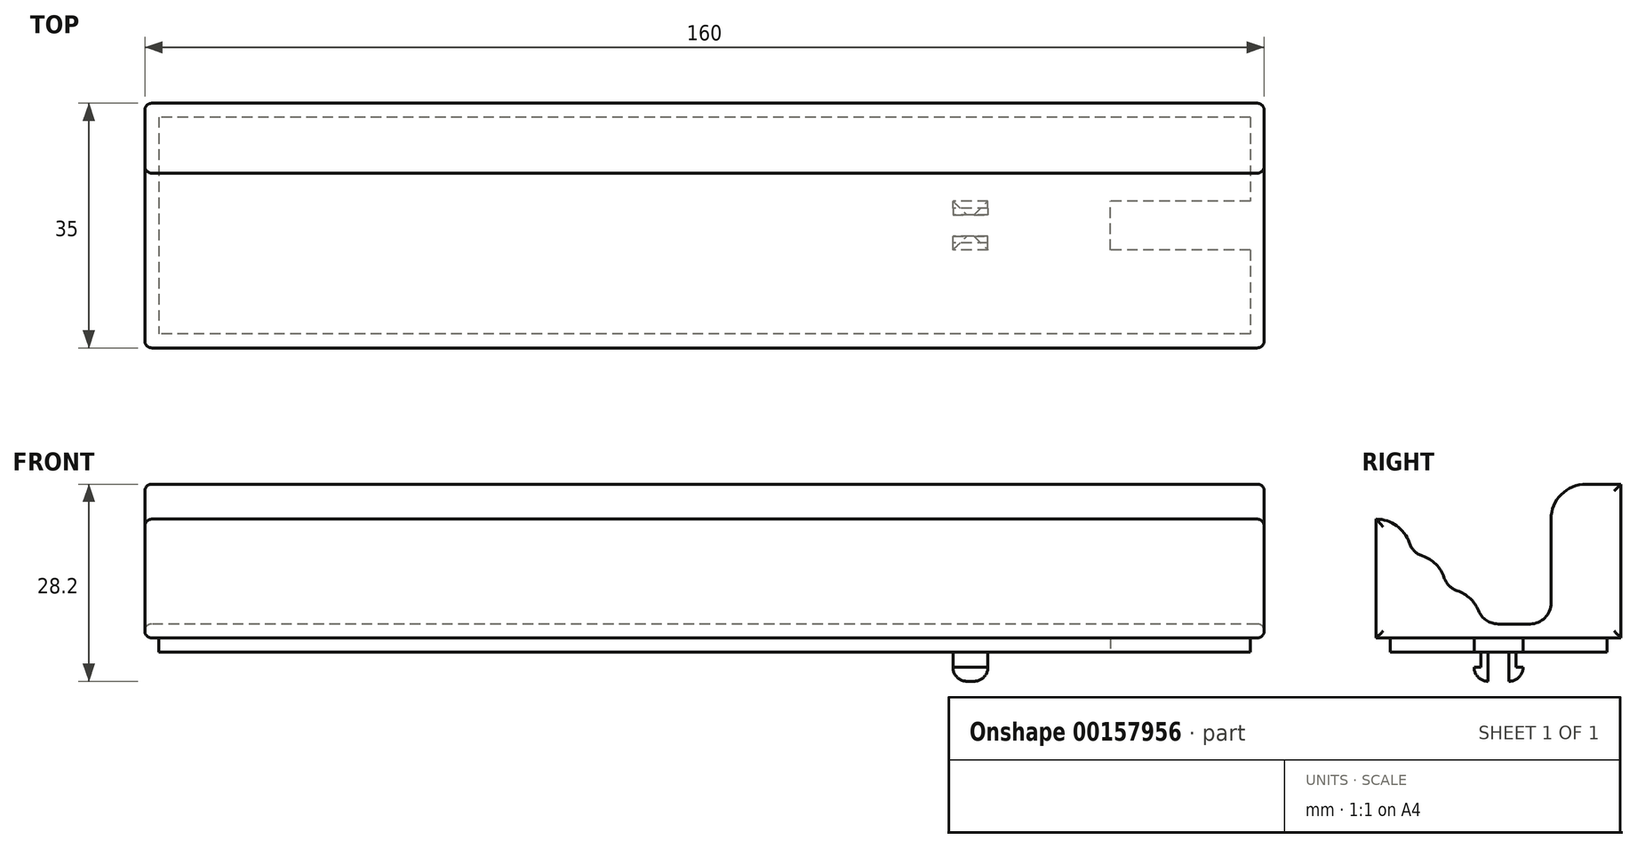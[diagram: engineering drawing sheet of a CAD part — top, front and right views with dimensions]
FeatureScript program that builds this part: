
annotation { "Feature Type Name" : "Feature", "Feature Type Description" : "" }
export const myFeature = defineFeature(function(context is Context, id is Id, definition is map)
    precondition{}
    {
        {
            var Q0;
            Q0=qCreatedBy(makeId("Right.planeOp"),FACE);
            var sketch = newSketch(context, id + "F0", { "sketchPlane" : qUnion([Q0])});
            skPoint(sketch, "E0.middle", {"position": v(0, 0) * mm});
            skLineSegment(sketch, "E1", {"start": v(18.73, 20.16) * mm, "end": v(18.73, 20.16) * mm});
            skLineSegment(sketch, "E2.bottom", {"start": v(13.13, 38.98) * mm, "end": v(22.1, 38.98) * mm});
            skPoint(sketch, "E3.visualSharp", {"position": v(11.13, 38.98) * mm});
            skArc(sketch, "E3.filletArc", {"start": v(13.13, 38.98) * mm, "mid": v(11.72, 38.4) * mm, "end": v(11.13, 36.98) * mm});
            skLineSegment(sketch, "E4.bottom", {"start": v(17.5, 1) * mm, "end": v(-17.5, 1) * mm});
            skLineSegment(sketch, "E4.top", {"start": v(17.5, -1) * mm, "end": v(-17.5, -1) * mm});
            skLineSegment(sketch, "E4.left", {"start": v(17.5, 1) * mm, "end": v(17.5, -1) * mm});
            skLineSegment(sketch, "E4.right", {"start": v(-17.5, 1) * mm, "end": v(-17.5, -1) * mm});
            skLineSegment(sketch, "E5.bottom", {"start": v(17.5, 1) * mm, "end": v(7.5, 1) * mm});
            skLineSegment(sketch, "E5.top", {"start": v(17.5, 21) * mm, "end": v(12.5, 21) * mm});
            skLineSegment(sketch, "E5.left", {"start": v(17.5, 1) * mm, "end": v(17.5, 21) * mm});
            skLineSegment(sketch, "E5.right", {"start": v(7.5, 1) * mm, "end": v(7.5, 16) * mm});
            skLineSegment(sketch, "E6.bottom", {"start": v(-17.5, 1) * mm, "end": v(-12.5, 1) * mm});
            skLineSegment(sketch, "E6.top", {"start": v(-17.5, 16) * mm, "end": v(-17.5, 16) * mm});
            skLineSegment(sketch, "E6.left", {"start": v(-17.5, 1) * mm, "end": v(-17.5, 16) * mm});
            skLineSegment(sketch, "E6.right", {"start": v(-12.5, 1) * mm, "end": v(-12.5, 11) * mm});
            skLineSegment(sketch, "E7.bottom", {"start": v(-12.5, 11) * mm, "end": v(-12.5, 11) * mm});
            skLineSegment(sketch, "E7.top", {"start": v(-12.5, 1) * mm, "end": v(-7.5, 1) * mm});
            skLineSegment(sketch, "E7.left", {"start": v(-12.5, 11) * mm, "end": v(-12.5, 1) * mm});
            skLineSegment(sketch, "E7.right", {"start": v(-7.5, 6) * mm, "end": v(-7.5, 1) * mm});
            skLineSegment(sketch, "E8.bottom", {"start": v(-7.5, 6) * mm, "end": v(-7.5, 6) * mm});
            skLineSegment(sketch, "E8.top", {"start": v(-7.5, 1) * mm, "end": v(-2.5, 1) * mm});
            skLineSegment(sketch, "E8.right", {"start": v(-2.5, 1) * mm, "end": v(-2.5, 1) * mm});
            skPoint(sketch, "E9.visualSharp", {"position": v(7.5, 21) * mm});
            skArc(sketch, "E9.filletArc", {"start": v(12.5, 21) * mm, "mid": v(8.96, 19.54) * mm, "end": v(7.5, 16) * mm});
            skPoint(sketch, "E10.visualSharp", {"position": v(-2.5, 6) * mm});
            skArc(sketch, "E10.filletArc", {"start": v(-2.5, 1) * mm, "mid": v(-3.96, 4.54) * mm, "end": v(-7.5, 6) * mm});
            skPoint(sketch, "E11.visualSharp", {"position": v(-7.5, 11) * mm});
            skArc(sketch, "E11.filletArc", {"start": v(-7.5, 6) * mm, "mid": v(-8.96, 9.54) * mm, "end": v(-12.5, 11) * mm});
            skPoint(sketch, "E12.visualSharp", {"position": v(-12.5, 16) * mm});
            skArc(sketch, "E12.filletArc", {"start": v(-12.5, 11) * mm, "mid": v(-13.96, 14.54) * mm, "end": v(-17.5, 16) * mm});
            skSolve(sketch);
        }
        {
            var Q0;
            Q0=makeQuery(id+"F0.imprint","IMPRINT",FACE,{"disambiguationData":[TD([[makeQuery(id+"F0.imprint","IMPRINT",EDGE,{"derivedFrom":sQuery(id+"F0.wireOp",EDGE,"E5.top")}),1.0]])]});
            var Q1;
            Q1=makeQuery(id+"F0.imprint","IMPRINT",FACE,{"disambiguationData":[TD([[makeQuery(id+"F0.imprint","IMPRINT",EDGE,{"derivedFrom":sQuery(id+"F0.wireOp",EDGE,"E4.top")}),-1.0]])]});
            var Q2;
            {var subQ0=sQuery(id+"F0.wireOp",EDGE,"E6.left");Q2=makeQuery(id+"F0.imprint","IMPRINT",FACE,{"disambiguationData":[TD([[makeQuery(id+"F0.imprint","IMPRINT",EDGE,{"derivedFrom":subQ0}),-1.0]])]});}
            var Q3;
            {var subQ2=sQuery(id+"F0.wireOp",EDGE,"E6.right");Q3=makeQuery(id+"F0.imprint","IMPRINT",FACE,{"disambiguationData":[TD([[makeQuery(id+"F0.imprint","IMPRINT",EDGE,{"derivedFrom":subQ2}),-1.0]])]});}
            var Q4;
            {var subQ0=sQuery(id+"F0.wireOp",EDGE,"E7.right");Q4=makeQuery(id+"F0.imprint","IMPRINT",FACE,{"disambiguationData":[TD([[makeQuery(id+"F0.imprint","IMPRINT",EDGE,{"derivedFrom":subQ0}),1.0]])]});}
            extrude(context, id + "F1", {"entities" : qUnion([Q0, Q1, Q2, Q3, Q4]), "endBound" : BoundingType.SYMMETRIC, "depth" : 160 * mm});
        }
        {
            var Q0;
            Q0=makeQuery(id+"F1.opExtrude","SWEPT_FACE",FACE,{"disambiguationData":[OSD([sQuery(id+"F0.wireOp",EDGE,"E4.top")])]});
            var sketch = newSketch(context, id + "F2", { "sketchPlane" : qUnion([Q0])});
            skLineSegment(sketch, "E13.bottom", {"start": v(78, -15.5) * mm, "end": v(-78, -15.5) * mm});
            skLineSegment(sketch, "E13.top", {"start": v(78, 15.5) * mm, "end": v(-78, 15.5) * mm});
            skLineSegment(sketch, "E13.left", {"start": v(78, -15.5) * mm, "end": v(78, 15.5) * mm});
            skLineSegment(sketch, "E13.right", {"start": v(-78, -15.5) * mm, "end": v(-78, 15.5) * mm});
            skPoint(sketch, "E13.middle", {"position": v(0, 0) * mm});
            skSolve(sketch);
        }
        {
            var Q0;
            Q0=qSketchRegion(id+"F2",true);
            extrude(context, id + "F3", {"entities" : qUnion([Q0]), "operationType" : NewBodyOperationType.ADD, "depth" : 2 * mm});
        }
        {
            var Q0;
            Q0=makeQuery(id+"F3.opExtrude","CAP_FACE",FACE,{"disambiguationData":[OSD([sQuery(id+"F2.wireOp",EDGE,"E13.bottom"),sQuery(id+"F2.wireOp",EDGE,"E13.top"),sQuery(id+"F2.wireOp",EDGE,"E13.left"),sQuery(id+"F2.wireOp",EDGE,"E13.right")])],"isStart":false});
            var sketch = newSketch(context, id + "F4", { "sketchPlane" : qUnion([Q0])});
            skLineSegment(sketch, "E14.bottom", {"start": v(40.5, -2.5) * mm, "end": v(35.5, -2.5) * mm});
            skLineSegment(sketch, "E14.top", {"start": v(40.5, 2.5) * mm, "end": v(35.5, 2.5) * mm});
            skLineSegment(sketch, "E14.left", {"start": v(40.5, -2.5) * mm, "end": v(40.5, 2.5) * mm});
            skLineSegment(sketch, "E14.right", {"start": v(35.5, -2.5) * mm, "end": v(35.5, 2.5) * mm});
            skPoint(sketch, "E14.middle", {"position": v(38, 0) * mm});
            skPoint(sketch, "E15", {"position": v(78, -0.48) * mm});
            skSolve(sketch);
        }
        {
            var Q0;
            Q0=qSketchRegion(id+"F4",true);
            extrude(context, id + "F5", {"entities" : qUnion([Q0]), "operationType" : NewBodyOperationType.ADD, "depth" : 2.2 * mm});
        }
        {
            var Q0;
            Q0=makeQuery(id+"F5.opExtrude","CAP_FACE",FACE,{"disambiguationData":[OSD([sQuery(id+"F4.wireOp",EDGE,"E14.bottom"),sQuery(id+"F4.wireOp",EDGE,"E14.top"),sQuery(id+"F4.wireOp",EDGE,"E14.left"),sQuery(id+"F4.wireOp",EDGE,"E14.right")])],"isStart":false});
            var sketch = newSketch(context, id + "F6", { "sketchPlane" : qUnion([Q0])});
            skLineSegment(sketch, "E16.bottom", {"start": v(40.5, 3.5) * mm, "end": v(35.5, 3.5) * mm});
            skLineSegment(sketch, "E16.top", {"start": v(40.5, -3.5) * mm, "end": v(35.5, -3.5) * mm});
            skLineSegment(sketch, "E16.left", {"start": v(35.5, 3.5) * mm, "end": v(35.5, -3.5) * mm});
            skLineSegment(sketch, "E16.right", {"start": v(40.5, 3.5) * mm, "end": v(40.5, -3.5) * mm});
            skPoint(sketch, "E16.middle.positionSnap0", {"position": v(40.5, 0) * mm});
            skPoint(sketch, "E16.centerSnap0", {"position": v(40.5, 0) * mm});
            skPoint(sketch, "E17", {"position": v(35.5, 0) * mm});
            skSolve(sketch);
        }
        {
            var Q0;
            Q0=qSketchRegion(id+"F6",true);
            extrude(context, id + "F7", {"entities" : qUnion([Q0]), "operationType" : NewBodyOperationType.ADD, "depth" : 2 * mm});
        }
        {
            var Q0;
            Q0=makeQuery(id+"F7.opExtrude","CAP_FACE",FACE,{"disambiguationData":[OSD([sQuery(id+"F6.wireOp",EDGE,"E16.bottom"),sQuery(id+"F6.wireOp",EDGE,"E16.top"),sQuery(id+"F6.wireOp",EDGE,"E16.left"),sQuery(id+"F6.wireOp",EDGE,"E16.right")])],"isStart":false});
            var sketch = newSketch(context, id + "F8", { "sketchPlane" : qUnion([Q0])});
            skLineSegment(sketch, "E18.bottom", {"start": v(40.5, 1.5) * mm, "end": v(35.5, 1.5) * mm});
            skLineSegment(sketch, "E18.top", {"start": v(40.5, -1.5) * mm, "end": v(35.5, -1.5) * mm});
            skLineSegment(sketch, "E18.left", {"start": v(35.5, 1.5) * mm, "end": v(35.5, -1.5) * mm});
            skLineSegment(sketch, "E18.right", {"start": v(40.5, 1.5) * mm, "end": v(40.5, -1.5) * mm});
            skLineSegment(sketch, "E19.bottom", {"start": v(39.5, -3.5) * mm, "end": v(36.5, -3.5) * mm});
            skSolve(sketch);
        }
        {
            var Q0;
            Q0=makeQuery(id+"F8.imprint","IMPRINT",FACE,{"disambiguationData":[TD([[makeQuery(id+"F8.imprint","IMPRINT",EDGE,{"derivedFrom":sQuery(id+"F8.wireOp",EDGE,"E18.bottom")}),1.0]])]});
            extrude(context, id + "F9", {"entities" : qUnion([Q0]), "operationType" : NewBodyOperationType.REMOVE, "oppositeDirection" : true, "depth" : 4.2 * mm});
        }
        {
            var Q0;
            {var subQ0=sQuery(id+"F6.wireOp",EDGE,"E16.right");var subQ1=sQuery(id+"F6.wireOp",EDGE,"E16.top");var subQ3=makeQuery(id+"F7.opExtrude","CAP_EDGE",EDGE,{"disambiguationData":[OSD([subQ0])],"isStart":false});Q0=makeQuery(id+"F9.boolean.opBoolean","SPLIT",EDGE,{"disambiguationData":[TD([makeQuery(id+"F7.opExtrude","SWEPT_FACE",FACE,{"disambiguationData":[OSD([subQ1])]})])],"derivedFrom":subQ3});}
            var Q1;
            {var subQ0=sQuery(id+"F6.wireOp",EDGE,"E16.right");var subQ1=sQuery(id+"F6.wireOp",EDGE,"E16.top");var subQ3=makeQuery(id+"F7.opExtrude","CAP_EDGE",EDGE,{"disambiguationData":[OSD([subQ1])],"isStart":false});Q1=makeQuery(id+"F9.boolean.opBoolean","SPLIT",EDGE,{"disambiguationData":[TD([makeQuery(id+"F7.opExtrude","SWEPT_FACE",FACE,{"disambiguationData":[OSD([subQ0])]})])],"derivedFrom":subQ3});}
            var Q2;
            {var subQ0=sQuery(id+"F6.wireOp",EDGE,"E16.bottom");var subQ1=sQuery(id+"F6.wireOp",EDGE,"E16.right");var subQ3=makeQuery(id+"F7.opExtrude","CAP_EDGE",EDGE,{"disambiguationData":[OSD([subQ1])],"isStart":false});Q2=makeQuery(id+"F9.boolean.opBoolean","SPLIT",EDGE,{"disambiguationData":[TD([makeQuery(id+"F7.opExtrude","SWEPT_FACE",FACE,{"disambiguationData":[OSD([subQ0])]})])],"derivedFrom":subQ3});}
            var Q3;
            {var subQ0=sQuery(id+"F6.wireOp",EDGE,"E16.bottom");var subQ1=sQuery(id+"F6.wireOp",EDGE,"E16.right");var subQ3=makeQuery(id+"F7.opExtrude","CAP_EDGE",EDGE,{"disambiguationData":[OSD([subQ0])],"isStart":false});Q3=makeQuery(id+"F9.boolean.opBoolean","SPLIT",EDGE,{"disambiguationData":[TD([makeQuery(id+"F7.opExtrude","SWEPT_FACE",FACE,{"disambiguationData":[OSD([subQ1])]})])],"derivedFrom":subQ3});}
            var Q4;
            {var subQ0=sQuery(id+"F6.wireOp",EDGE,"E16.bottom");var subQ1=sQuery(id+"F6.wireOp",EDGE,"E16.left");var subQ3=makeQuery(id+"F7.opExtrude","CAP_EDGE",EDGE,{"disambiguationData":[OSD([subQ0])],"isStart":false});Q4=makeQuery(id+"F9.boolean.opBoolean","SPLIT",EDGE,{"disambiguationData":[TD([makeQuery(id+"F7.opExtrude","SWEPT_FACE",FACE,{"disambiguationData":[OSD([subQ1])]})])],"derivedFrom":subQ3});}
            var Q5;
            {var subQ0=sQuery(id+"F6.wireOp",EDGE,"E16.bottom");var subQ1=sQuery(id+"F6.wireOp",EDGE,"E16.left");var subQ3=makeQuery(id+"F7.opExtrude","CAP_EDGE",EDGE,{"disambiguationData":[OSD([subQ1])],"isStart":false});Q5=makeQuery(id+"F9.boolean.opBoolean","SPLIT",EDGE,{"disambiguationData":[TD([makeQuery(id+"F7.opExtrude","SWEPT_FACE",FACE,{"disambiguationData":[OSD([subQ0])]})])],"derivedFrom":subQ3});}
            var Q6;
            {var subQ0=sQuery(id+"F6.wireOp",EDGE,"E16.left");var subQ1=sQuery(id+"F6.wireOp",EDGE,"E16.top");var subQ3=makeQuery(id+"F7.opExtrude","CAP_EDGE",EDGE,{"disambiguationData":[OSD([subQ0])],"isStart":false});Q6=makeQuery(id+"F9.boolean.opBoolean","SPLIT",EDGE,{"disambiguationData":[TD([makeQuery(id+"F7.opExtrude","SWEPT_FACE",FACE,{"disambiguationData":[OSD([subQ1])]})])],"derivedFrom":subQ3});}
            var Q7;
            {var subQ0=sQuery(id+"F6.wireOp",EDGE,"E16.left");var subQ1=sQuery(id+"F6.wireOp",EDGE,"E16.top");var subQ3=makeQuery(id+"F7.opExtrude","CAP_EDGE",EDGE,{"disambiguationData":[OSD([subQ1])],"isStart":false});Q7=makeQuery(id+"F9.boolean.opBoolean","SPLIT",EDGE,{"disambiguationData":[TD([makeQuery(id+"F7.opExtrude","SWEPT_FACE",FACE,{"disambiguationData":[OSD([subQ0])]})])],"derivedFrom":subQ3});}
            fillet(context, id + "F10", {"entities" : qUnion([Q0, Q1, Q2, Q3, Q4, Q5, Q6, Q7]), "radius" : 2 * mm, "tangentPropagation" : true, "allowEdgeOverflow" : false});
        }
        {
            var Q0;
            Q0=makeQuery(id+"F9.boolean.opBoolean","MERGE",FACE,{"derivedFrom":[makeQuery(id+"F3.opExtrude","CAP_FACE",FACE,{"disambiguationData":[OSD([sQuery(id+"F2.wireOp",EDGE,"E13.bottom"),sQuery(id+"F2.wireOp",EDGE,"E13.top"),sQuery(id+"F2.wireOp",EDGE,"E13.left"),sQuery(id+"F2.wireOp",EDGE,"E13.right")])],"isStart":false}),makeQuery(id+"F9.opExtrude","CAP_FACE",FACE,{"disambiguationData":[OSD([sQuery(id+"F8.wireOp",EDGE,"E18.bottom"),sQuery(id+"F8.wireOp",EDGE,"E18.top"),sQuery(id+"F8.wireOp",EDGE,"E18.left"),sQuery(id+"F8.wireOp",EDGE,"E18.right")])],"isStart":false})]});
            var sketch = newSketch(context, id + "F11", { "sketchPlane" : qUnion([Q0])});
            skLineSegment(sketch, "E20.bottom", {"start": v(78, 3.5) * mm, "end": v(58, 3.5) * mm});
            skLineSegment(sketch, "E20.top", {"start": v(78, -3.5) * mm, "end": v(58, -3.5) * mm});
            skLineSegment(sketch, "E20.left", {"start": v(78, 3.5) * mm, "end": v(78, -3.5) * mm});
            skLineSegment(sketch, "E20.right", {"start": v(58, 3.5) * mm, "end": v(58, -3.5) * mm});
            skPoint(sketch, "E20.middle", {"position": v(68, 0) * mm});
            skSolve(sketch);
        }
        {
            var Q0;
            Q0=qSketchRegion(id+"F11",true);
            extrude(context, id + "F12", {"entities" : qUnion([Q0]), "operationType" : NewBodyOperationType.REMOVE, "oppositeDirection" : true, "depth" : 2 * mm});
        }
        {
            var Q0;
            Q0=makeQuery(id+"F1.opExtrude","SWEPT_EDGE",EDGE,{"disambiguationData":[OSD([sQuery(id+"F0.wireOp",EDGE,"E6.right"),sQuery(id+"F0.wireOp",EDGE,"E11.filletArc"),sQuery(id+"F0.wireOp",EDGE,"E12.filletArc")])]});
            var Q1;
            Q1=makeQuery(id+"F1.opExtrude","SWEPT_EDGE",EDGE,{"disambiguationData":[OSD([sQuery(id+"F0.wireOp",EDGE,"E7.right"),sQuery(id+"F0.wireOp",EDGE,"E10.filletArc"),sQuery(id+"F0.wireOp",EDGE,"E11.filletArc")])]});
            var Q2;
            Q2=makeQuery(id+"F1.opExtrude","SWEPT_EDGE",EDGE,{"disambiguationData":[OSD([sQuery(id+"F0.wireOp",EDGE,"E4.bottom"),sQuery(id+"F0.wireOp",EDGE,"E10.filletArc")])]});
            var Q3;
            Q3=makeQuery(id+"F1.opExtrude","SWEPT_EDGE",EDGE,{"disambiguationData":[OSD([sQuery(id+"F0.wireOp",EDGE,"E4.bottom"),sQuery(id+"F0.wireOp",EDGE,"E5.right")])]});
            fillet(context, id + "F13", {"entities" : qUnion([Q0, Q1, Q2, Q3]), "radius" : 3 * mm, "tangentPropagation" : true, "allowEdgeOverflow" : false});
        }
        {
            var Q0;
            Q0=makeQuery(id+"F1.opExtrude","CAP_FACE",FACE,{"disambiguationData":[OSD([sQuery(id+"F0.wireOp",EDGE,"E4.bottom"),sQuery(id+"F0.wireOp",EDGE,"E4.top"),sQuery(id+"F0.wireOp",EDGE,"E4.left"),sQuery(id+"F0.wireOp",EDGE,"E4.right"),sQuery(id+"F0.wireOp",EDGE,"E5.top"),sQuery(id+"F0.wireOp",EDGE,"E5.left"),sQuery(id+"F0.wireOp",EDGE,"E5.right"),sQuery(id+"F0.wireOp",EDGE,"E6.left"),sQuery(id+"F0.wireOp",EDGE,"E9.filletArc"),sQuery(id+"F0.wireOp",EDGE,"E10.filletArc"),sQuery(id+"F0.wireOp",EDGE,"E11.filletArc"),sQuery(id+"F0.wireOp",EDGE,"E12.filletArc")])],"isStart":false});
            var Q1;
            Q1=makeQuery(id+"F1.opExtrude","CAP_FACE",FACE,{"disambiguationData":[OSD([sQuery(id+"F0.wireOp",EDGE,"E4.bottom"),sQuery(id+"F0.wireOp",EDGE,"E4.top"),sQuery(id+"F0.wireOp",EDGE,"E4.left"),sQuery(id+"F0.wireOp",EDGE,"E4.right"),sQuery(id+"F0.wireOp",EDGE,"E5.top"),sQuery(id+"F0.wireOp",EDGE,"E5.left"),sQuery(id+"F0.wireOp",EDGE,"E5.right"),sQuery(id+"F0.wireOp",EDGE,"E6.left"),sQuery(id+"F0.wireOp",EDGE,"E9.filletArc"),sQuery(id+"F0.wireOp",EDGE,"E10.filletArc"),sQuery(id+"F0.wireOp",EDGE,"E11.filletArc"),sQuery(id+"F0.wireOp",EDGE,"E12.filletArc")])],"isStart":true});
            fillet(context, id + "F14", {"entities" : qUnion([Q0, Q1]), "radius" : 1 * mm, "tangentPropagation" : true, "allowEdgeOverflow" : false});
        }
    });
